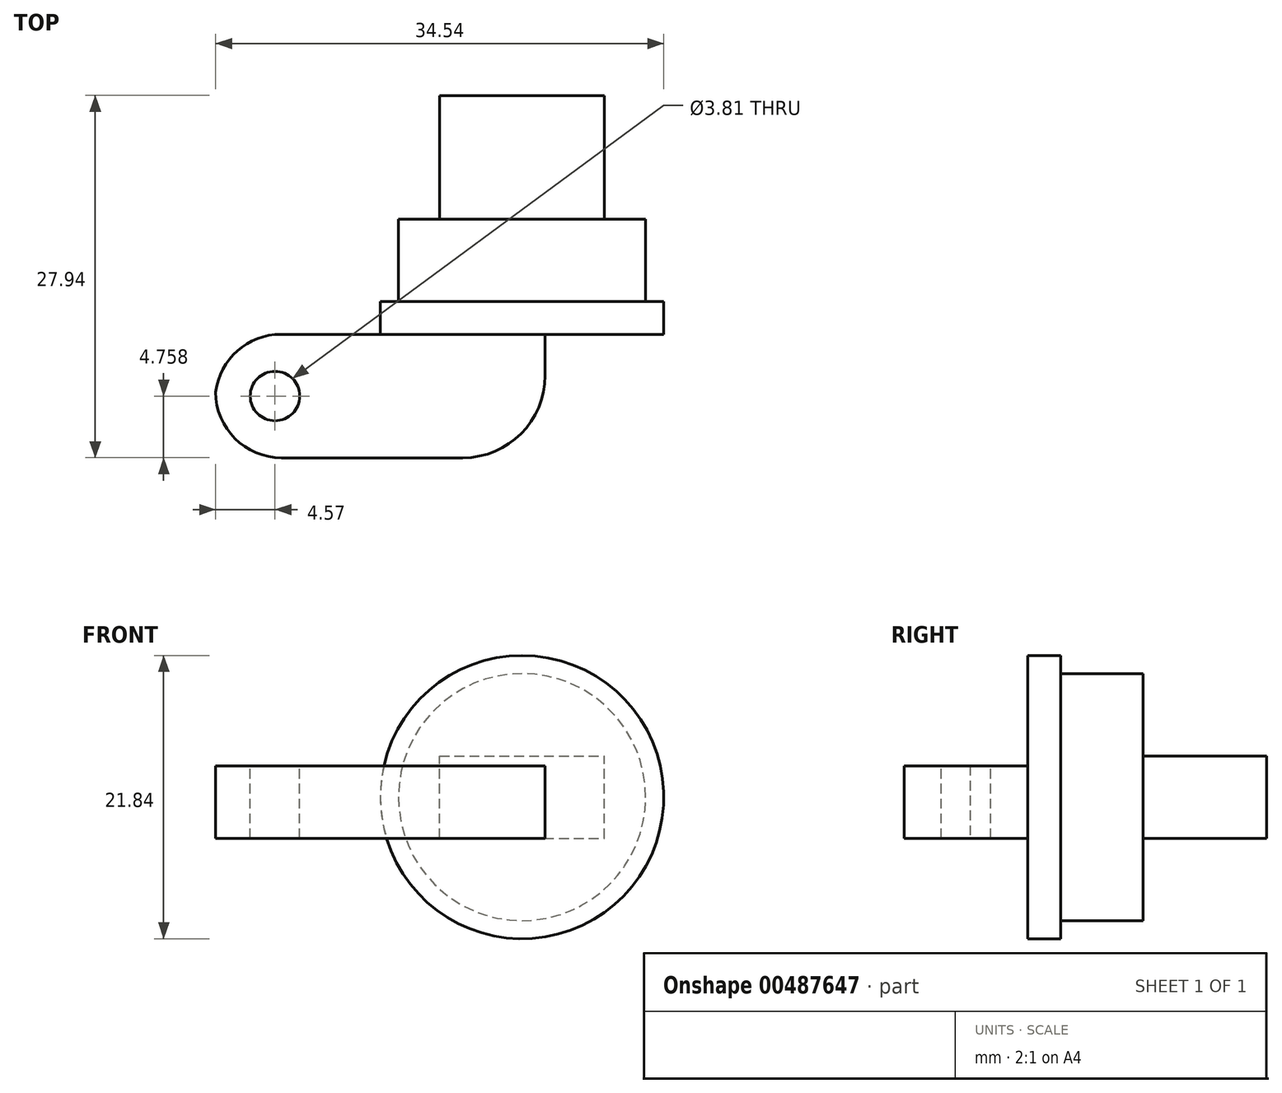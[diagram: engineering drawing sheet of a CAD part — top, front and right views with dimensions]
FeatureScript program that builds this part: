
annotation { "Feature Type Name" : "Feature", "Feature Type Description" : "" }
export const myFeature = defineFeature(function(context is Context, id is Id, definition is map)
    precondition{}
    {
        {
            var Q0;
            Q0=qCreatedBy(makeId("Front.planeOp"),FACE);
            var sketch = newSketch(context, id + "F0", { "sketchPlane" : qUnion([Q0])});
            skCircle(sketch, "E0", {"center": v(0, 0) * mm, "radius": 9.53 * mm});
            skSolve(sketch);
        }
        {
            var Q0;
            Q0 = qSketchRegion(id + "F0", true);
            extrude(context, id + "F1", {"entities" : qUnion([Q0]), "depth" : 6.35 * mm, "offsetDistance" : 25.4 * mm});
        }
        {
            var Q0;
            Q0=makeQuery(id+"F1.opExtrude","CAP_FACE",FACE,{"disambiguationData":[OSD([sQuery(id+"F0.wireOp",EDGE,"E0")])],"isStart":true});
            var sketch = newSketch(context, id + "F2", { "sketchPlane" : qUnion([Q0])});
            skLineSegment(sketch, "E1", {"start": v(0, 0) * mm, "end": v(16.94, 0) * mm, "construction": true});
            skLineSegment(sketch, "E2", {"start": v(0, 0) * mm, "end": v(0, -14) * mm, "construction": true});
            skLineSegment(sketch, "E3", {"start": v(6.35, -3.18) * mm, "end": v(6.35, 3.17) * mm});
            skLineSegment(sketch, "E4", {"start": v(-6.35, -3.18) * mm, "end": v(-6.35, 3.17) * mm});
            skLineSegment(sketch, "E5", {"start": v(6.35, -3.18) * mm, "end": v(-6.35, -3.18) * mm});
            skLineSegment(sketch, "E6", {"start": v(6.35, 3.17) * mm, "end": v(-6.35, 3.17) * mm});
            skPoint(sketch, "E7.orphan", {"position": v(6.35, -14) * mm});
            skPoint(sketch, "E8.orphan", {"position": v(-6.35, -14) * mm});
            skSolve(sketch);
        }
        {
            var Q0;
            Q0=makeQuery(id+"F2.imprint","IMPRINT",FACE,{"disambiguationData":[TD([[makeQuery(id+"F2.imprint","IMPRINT",EDGE,{"derivedFrom":sQuery(id+"F2.wireOp",EDGE,"E3")}),1.0]])]});
            var Q1;
            Q1=sQuery(id+"F2.wireOp",EDGE,"E3");
            var Q2;
            Q2=sQuery(id+"F2.wireOp",EDGE,"E5");
            var Q3;
            Q3=sQuery(id+"F2.wireOp",EDGE,"E6");
            var Q4;
            Q4=sQuery(id+"F2.wireOp",EDGE,"E4");
            extrude(context, id + "F3", {"entities" : qUnion([Q0]), "operationType" : NewBodyOperationType.ADD, "surfaceOperationType" : NewSurfaceOperationType.ADD, "surfaceEntities" : qUnion([Q1, Q2, Q3, Q4]), "depth" : 9.52 * mm, "offsetDistance" : 25.4 * mm});
        }
        {
            var Q0;
            Q0=makeQuery(id+"F1.opExtrude","CAP_FACE",FACE,{"disambiguationData":[OSD([sQuery(id+"F0.wireOp",EDGE,"E0")])],"isStart":false});
            var sketch = newSketch(context, id + "F4", { "sketchPlane" : qUnion([Q0])});
            skCircle(sketch, "E9", {"center": v(0, 0) * mm, "radius": 10.92 * mm});
            skSolve(sketch);
        }
        {
            var Q0;
            Q0 = qSketchRegion(id + "F4", true);
            extrude(context, id + "F5", {"entities" : qUnion([Q0]), "operationType" : NewBodyOperationType.ADD, "depth" : 2.54 * mm, "offsetDistance" : 25.4 * mm});
        }
        {
            var Q0;
            Q0=makeQuery(id+"F5.opExtrude","CAP_FACE",FACE,{"disambiguationData":[OSD([sQuery(id+"F4.wireOp",EDGE,"E9")])],"isStart":false});
            var sketch = newSketch(context, id + "F6", { "sketchPlane" : qUnion([Q0])});
            skLineSegment(sketch, "E10.bottom", {"start": v(1.78, 2.41) * mm, "end": v(-23.62, 2.41) * mm});
            skLineSegment(sketch, "E10.top", {"start": v(1.78, -3.17) * mm, "end": v(-23.62, -3.18) * mm});
            skLineSegment(sketch, "E10.left", {"start": v(1.78, 2.41) * mm, "end": v(1.78, -3.18) * mm});
            skLineSegment(sketch, "E10.right", {"start": v(-23.62, 2.41) * mm, "end": v(-23.62, -3.18) * mm});
            skLineSegment(sketch, "E11", {"start": v(0, 0) * mm, "end": v(8.7, 0) * mm, "construction": true});
            skSolve(sketch);
        }
        {
            var Q0;
            Q0 = qSketchRegion(id + "F6", true);
            extrude(context, id + "F7", {"entities" : qUnion([Q0]), "operationType" : NewBodyOperationType.ADD, "depth" : 9.52 * mm, "offsetDistance" : 25.4 * mm});
        }
        {
            var Q0;
            Q0=makeQuery(id+"F7.opExtrude","CAP_EDGE",EDGE,{"disambiguationData":[OSD([sQuery(id+"F6.wireOp",EDGE,"E10.right")])],"isStart":false});
            fillet(context, id + "F8", {"entities" : qUnion([Q0]), "radius" : 5.08 * mm, "tangentPropagation" : true, "allowEdgeOverflow" : false});
        }
        {
            var Q0;
            Q0=makeQuery(id+"F7.opExtrude","CAP_EDGE",EDGE,{"disambiguationData":[OSD([sQuery(id+"F6.wireOp",EDGE,"E10.right")])],"isStart":true});
            fillet(context, id + "F9", {"entities" : qUnion([Q0]), "radius" : 5.08 * mm, "tangentPropagation" : true, "allowEdgeOverflow" : false});
        }
        {
            var Q0;
            Q0=makeQuery(id+"F7.opExtrude","CAP_EDGE",EDGE,{"disambiguationData":[OSD([sQuery(id+"F6.wireOp",EDGE,"E10.left")])],"isStart":false});
            fillet(context, id + "F10", {"entities" : qUnion([Q0]), "radius" : 6.35 * mm, "tangentPropagation" : true, "allowEdgeOverflow" : false});
        }
        {
            var Q0;
            Q0=makeQuery(id+"F7.opExtrude","SWEPT_FACE",FACE,{"disambiguationData":[OSD([sQuery(id+"F6.wireOp",EDGE,"E10.bottom")])]});
            var sketch = newSketch(context, id + "F11", { "sketchPlane" : qUnion([Q0])});
            skLineSegment(sketch, "E12", {"start": v(-19.05, -13.65) * mm, "end": v(24.11, -13.65) * mm, "construction": true});
            skCircle(sketch, "E13", {"center": v(-19.05, -13.65) * mm, "radius": 1.9 * mm});
            skLineSegment(sketch, "E14", {"start": v(-19.05, -13.65) * mm, "end": v(-19.05, -3.58) * mm, "construction": true});
            skSolve(sketch);
        }
        {
            var Q0;
            Q0 = qSketchRegion(id + "F11", true);
            extrude(context, id + "F12", {"entities" : qUnion([Q0]), "operationType" : NewBodyOperationType.REMOVE, "endBound" : BoundingType.THROUGH_ALL, "oppositeDirection" : true, "depth" : 25.4 * mm, "offsetDistance" : 25.4 * mm});
        }
    });
